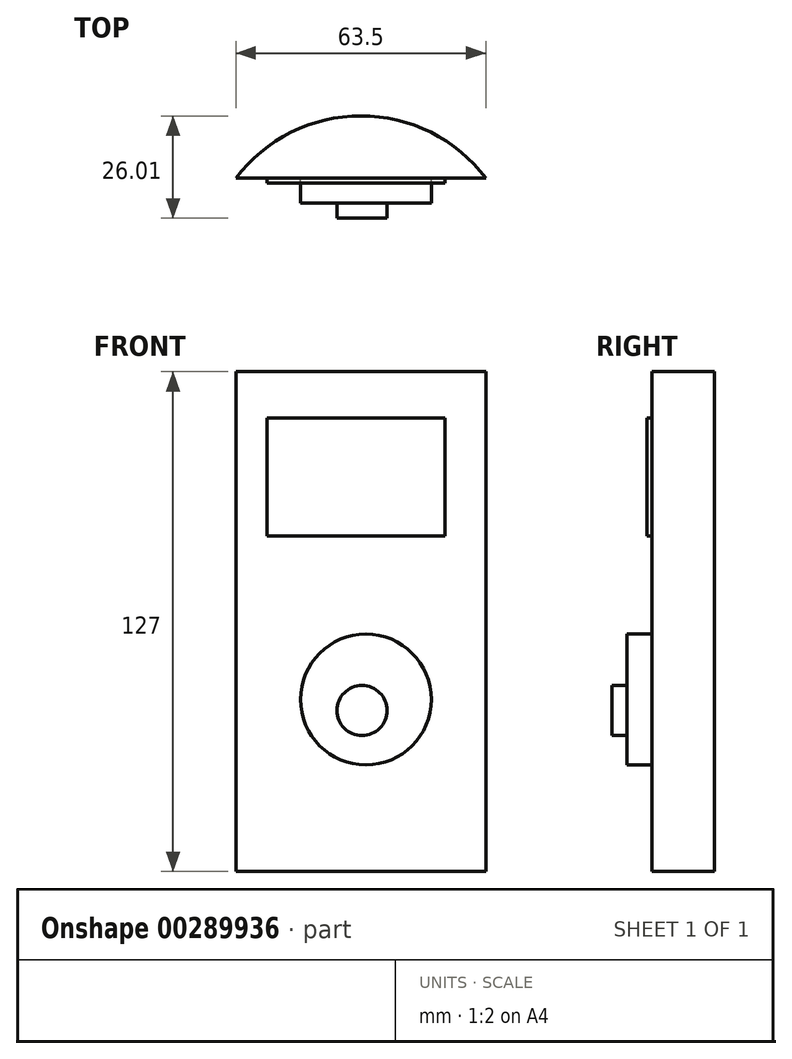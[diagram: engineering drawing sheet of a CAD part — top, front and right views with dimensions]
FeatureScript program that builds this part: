
annotation { "Feature Type Name" : "Feature", "Feature Type Description" : "" }
export const myFeature = defineFeature(function(context is Context, id is Id, definition is map)
    precondition{}
    {
        {
            var Q0;
            Q0=qCreatedBy(makeId("Top.planeOp"),FACE);
            var sketch = newSketch(context, id + "F0", { "sketchPlane" : qUnion([Q0])});
            skLineSegment(sketch, "E0", {"start": v(-39.15, 0) * mm, "end": v(24.35, 0) * mm});
            skArc(sketch, "E1", {"start": v(24.35, 0) * mm, "mid": v(-7.4, 15.85) * mm, "end": v(-39.15, 0) * mm});
            skSolve(sketch);
        }
        {
            var Q0;
            Q0 = qSketchRegion(id + "F0", true);
            extrude(context, id + "F1", {"entities" : qUnion([Q0]), "depth" : 127 * mm});
        }
        {
            var Q0;
            Q0=makeQuery(id+"F1.opExtrude","SWEPT_FACE",FACE,{"disambiguationData":[OSD([sQuery(id+"F0.wireOp",EDGE,"E0")])]});
            var sketch = newSketch(context, id + "F2", { "sketchPlane" : qUnion([Q0])});
            skCircle(sketch, "E2", {"center": v(-6.13, 43.73) * mm, "radius": 16.63 * mm});
            skSolve(sketch);
        }
        {
            var Q0;
            Q0 = qSketchRegion(id + "F2", true);
            extrude(context, id + "F3", {"entities" : qUnion([Q0]), "operationType" : NewBodyOperationType.ADD, "depth" : 6.35 * mm});
        }
        {
            var Q0;
            Q0=makeQuery(id+"F3.opExtrude","CAP_FACE",FACE,{"disambiguationData":[OSD([sQuery(id+"F2.wireOp",EDGE,"E2")])],"isStart":false});
            var sketch = newSketch(context, id + "F4", { "sketchPlane" : qUnion([Q0])});
            skLineSegment(sketch, "E3.bottom", {"start": v(-16.8, 48.06) * mm, "end": v(-14, 48.06) * mm});
            skLineSegment(sketch, "E3.top", {"start": v(-16.8, 34.57) * mm, "end": v(-14, 34.57) * mm});
            skLineSegment(sketch, "E3.left", {"start": v(-16.8, 48.06) * mm, "end": v(-16.8, 34.57) * mm});
            skLineSegment(sketch, "E3.right", {"start": v(-14, 48.06) * mm, "end": v(-14, 34.57) * mm});
            skLineSegment(sketch, "E4.bottom", {"start": v(0, 48.06) * mm, "end": v(2.8, 48.06) * mm});
            skLineSegment(sketch, "E4.top", {"start": v(0, 34.06) * mm, "end": v(2.8, 34.06) * mm});
            skLineSegment(sketch, "E4.left", {"start": v(0, 48.06) * mm, "end": v(0, 34.06) * mm});
            skLineSegment(sketch, "E4.right", {"start": v(2.8, 48.06) * mm, "end": v(2.8, 34.06) * mm});
            skSolve(sketch);
        }
        {
            var Q0;
            Q0 = qSketchRegion(id + "F4", true);
            extrude(context, id + "F5", {"entities" : qUnion([Q0]), "operationType" : NewBodyOperationType.ADD, "oppositeDirection" : true, "depth" : 2.54 * mm});
        }
        {
            var Q0;
            Q0=makeQuery(id+"F3.opExtrude","CAP_FACE",FACE,{"disambiguationData":[OSD([sQuery(id+"F2.wireOp",EDGE,"E2")])],"isStart":false});
            var sketch = newSketch(context, id + "F6", { "sketchPlane" : qUnion([Q0])});
            skCircle(sketch, "E5", {"center": v(-7.13, 40.93) * mm, "radius": 6.37 * mm});
            skSolve(sketch);
        }
        {
            var Q0;
            Q0 = qSketchRegion(id + "F6", true);
            extrude(context, id + "F7", {"entities" : qUnion([Q0]), "operationType" : NewBodyOperationType.ADD, "depth" : 3.8 * mm});
        }
        {
            var Q0;
            Q0=makeQuery(id+"F1.opExtrude","SWEPT_FACE",FACE,{"disambiguationData":[OSD([sQuery(id+"F0.wireOp",EDGE,"E0")])]});
            var sketch = newSketch(context, id + "F8", { "sketchPlane" : qUnion([Q0])});
            skLineSegment(sketch, "E6.bottom", {"start": v(-9.67, 41.43) * mm, "end": v(-8.66, 41.43) * mm});
            skLineSegment(sketch, "E6.top", {"start": v(-9.67, 36.35) * mm, "end": v(-8.66, 36.35) * mm});
            skLineSegment(sketch, "E6.left", {"start": v(-9.67, 41.43) * mm, "end": v(-9.67, 36.35) * mm});
            skLineSegment(sketch, "E6.right", {"start": v(-8.66, 41.43) * mm, "end": v(-8.66, 36.35) * mm});
            skLineSegment(sketch, "E7.bottom", {"start": v(-4.58, 41.43) * mm, "end": v(-3.06, 41.43) * mm});
            skLineSegment(sketch, "E7.top", {"start": v(-4.58, 36.35) * mm, "end": v(-3.06, 36.35) * mm});
            skLineSegment(sketch, "E7.left", {"start": v(-4.58, 41.43) * mm, "end": v(-4.58, 36.35) * mm});
            skLineSegment(sketch, "E7.right", {"start": v(-3.06, 41.43) * mm, "end": v(-3.06, 36.35) * mm});
            skSolve(sketch);
        }
        {
            var Q0;
            Q0 = qSketchRegion(id + "F8", true);
            extrude(context, id + "F9", {"entities" : qUnion([Q0]), "operationType" : NewBodyOperationType.ADD, "depth" : 2.54 * mm});
        }
        {
            var Q0;
            Q0=makeQuery(id+"F1.opExtrude","SWEPT_FACE",FACE,{"disambiguationData":[OSD([sQuery(id+"F0.wireOp",EDGE,"E0")])]});
            var sketch = newSketch(context, id + "F10", { "sketchPlane" : qUnion([Q0])});
            skLineSegment(sketch, "E8.bottom", {"start": v(14, 85.23) * mm, "end": v(-31.32, 85.23) * mm});
            skLineSegment(sketch, "E8.top", {"start": v(14, 115.28) * mm, "end": v(-31.32, 115.28) * mm});
            skLineSegment(sketch, "E8.left", {"start": v(14, 85.23) * mm, "end": v(14, 115.28) * mm});
            skLineSegment(sketch, "E8.right", {"start": v(-31.32, 85.23) * mm, "end": v(-31.32, 115.28) * mm});
            skPoint(sketch, "E8.middle", {"position": v(-8.66, 100.25) * mm});
            skSolve(sketch);
        }
        {
            var Q0;
            Q0 = qSketchRegion(id + "F10", true);
            extrude(context, id + "F11", {"entities" : qUnion([Q0]), "operationType" : NewBodyOperationType.ADD, "depth" : 1.27 * mm});
        }
    });
